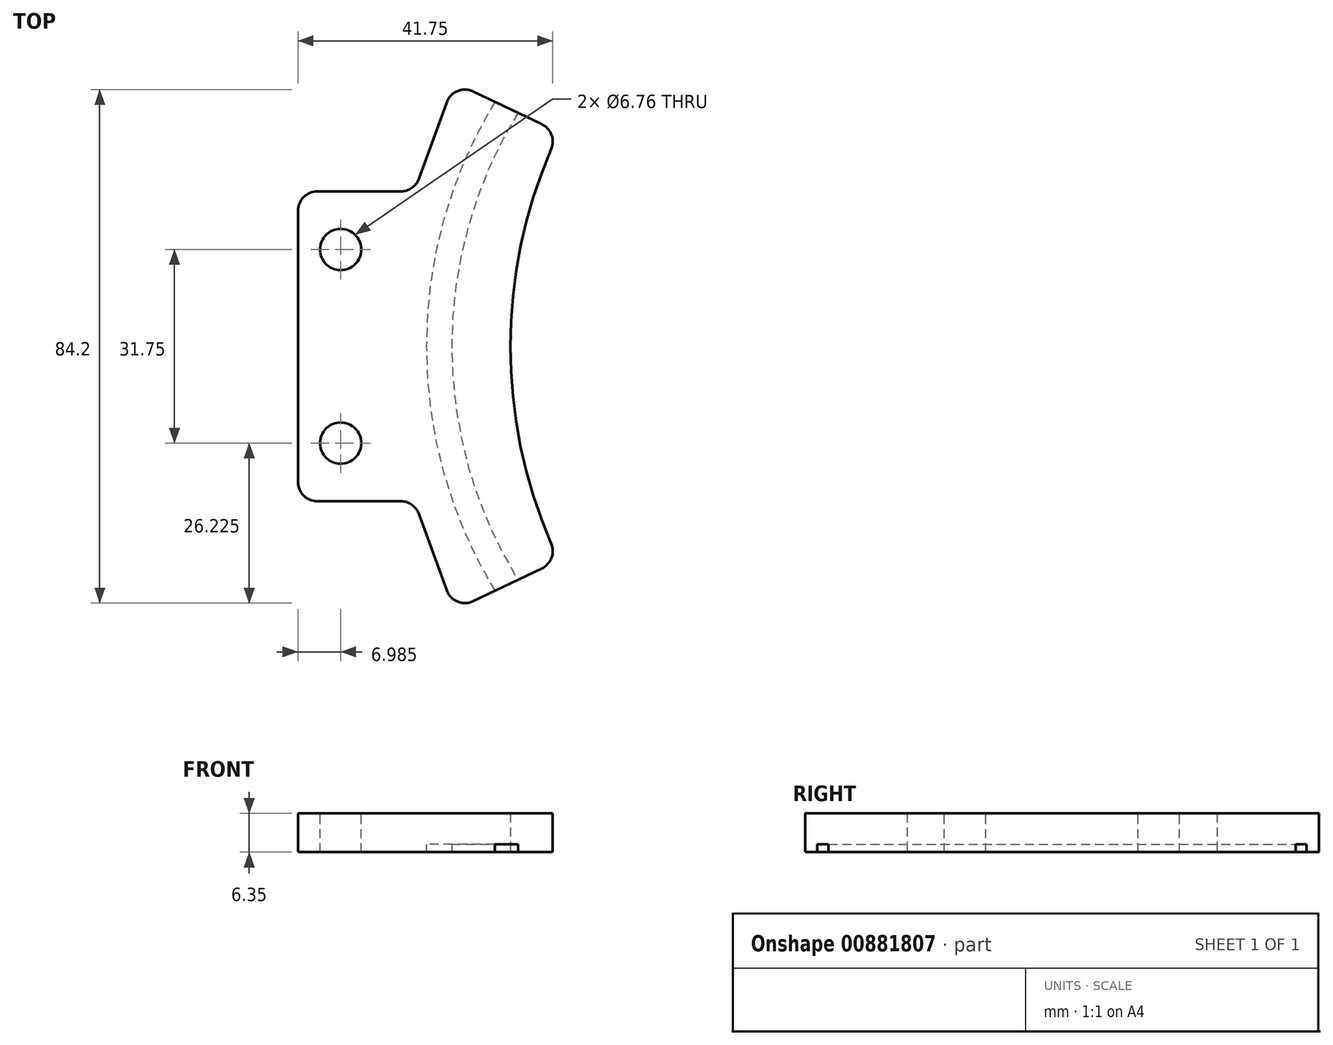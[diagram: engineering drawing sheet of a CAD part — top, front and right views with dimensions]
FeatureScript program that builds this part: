
annotation { "Feature Type Name" : "Feature", "Feature Type Description" : "" }
export const myFeature = defineFeature(function(context is Context, id is Id, definition is map)
    precondition{}
    {
        {
            var Q0;
            Q0=qCreatedBy(makeId("Top.planeOp"),FACE);
            var sketch = newSketch(context, id + "F0", { "sketchPlane" : qUnion([Q0])});
            skLineSegment(sketch, "E0", {"start": v(0, 25.4) * mm, "end": v(19.05, 25.4) * mm});
            skLineSegment(sketch, "E1", {"start": v(0, 25.4) * mm, "end": v(0, -25.4) * mm});
            skLineSegment(sketch, "E2", {"start": v(0, -25.4) * mm, "end": v(19.05, -25.4) * mm});
            skPoint(sketch, "E3", {"position": v(0, 0) * mm});
            skArc(sketch, "E4", {"start": v(42.76, 35.1) * mm, "mid": v(34.81, 0) * mm, "end": v(42.76, -35.1) * mm});
            skLineSegment(sketch, "E5", {"start": v(42.76, -35.1) * mm, "end": v(25.57, -43.3) * mm});
            skLineSegment(sketch, "E6", {"start": v(25.57, -43.3) * mm, "end": v(19.05, -25.4) * mm});
            skLineSegment(sketch, "E7", {"start": v(42.76, 35.1) * mm, "end": v(25.57, 43.3) * mm});
            skLineSegment(sketch, "E8", {"start": v(25.57, 43.3) * mm, "end": v(19.05, 25.4) * mm});
            skLineSegment(sketch, "E9", {"start": v(0, 0) * mm, "end": v(116.3, 0) * mm, "construction": true});
            skLineSegment(sketch, "E10", {"start": v(42.76, 35.1) * mm, "end": v(45.5, 40.83) * mm, "construction": true});
            skSolve(sketch);
        }
        {
            var Q0;
            Q0=makeQuery(id+"F0.imprint","IMPRINT",FACE,{"disambiguationData":[TD([[makeQuery(id+"F0.imprint","IMPRINT",EDGE,{"derivedFrom":sQuery(id+"F0.wireOp",EDGE,"E0")}),-1.0]])]});
            extrude(context, id + "F1", {"entities" : qUnion([Q0]), "depth" : 6.35 * mm, "offsetDistance" : 25.4 * mm});
        }
        {
            var Q0;
            Q0=makeQuery(id+"F1.opExtrude","CAP_FACE",FACE,{"disambiguationData":[OSD([sQuery(id+"F0.wireOp",EDGE,"E0"),sQuery(id+"F0.wireOp",EDGE,"E1"),sQuery(id+"F0.wireOp",EDGE,"E2"),sQuery(id+"F0.wireOp",EDGE,"E4"),sQuery(id+"F0.wireOp",EDGE,"E5"),sQuery(id+"F0.wireOp",EDGE,"E6"),sQuery(id+"F0.wireOp",EDGE,"E7"),sQuery(id+"F0.wireOp",EDGE,"E8")])],"isStart":true});
            var sketch = newSketch(context, id + "F2", { "sketchPlane" : qUnion([Q0])});
            skArc(sketch, "E11", {"start": v(34.16, 39.2) * mm, "mid": v(23.13, 0) * mm, "end": v(34.16, -39.2) * mm, "construction": true});
            skArc(sketch, "E12.0", {"start": v(32.27, 40.1) * mm, "mid": v(21.04, 0) * mm, "end": v(32.27, -40.1) * mm});
            skArc(sketch, "E13.0", {"start": v(36.05, 38.3) * mm, "mid": v(25.2, 0) * mm, "end": v(36.05, -38.3) * mm});
            skLineSegment(sketch, "E14", {"start": v(32.27, 40.1) * mm, "end": v(36.05, 38.3) * mm});
            skLineSegment(sketch, "E15", {"start": v(32.27, -40.1) * mm, "end": v(36.05, -38.3) * mm});
            skSolve(sketch);
        }
        {
            var Q0;
            Q0=makeQuery(id+"F2.imprint","IMPRINT",FACE,{"disambiguationData":[TD([[makeQuery(id+"F2.imprint","IMPRINT",EDGE,{"derivedFrom":sQuery(id+"F2.wireOp",EDGE,"E12.0")}),1.0]])]});
            extrude(context, id + "F3", {"entities" : qUnion([Q0]), "operationType" : NewBodyOperationType.REMOVE, "oppositeDirection" : true, "depth" : 1.27 * mm, "offsetDistance" : 25.4 * mm});
        }
        {
            var Q0;
            Q0=makeQuery(id+"F1.opExtrude","CAP_FACE",FACE,{"disambiguationData":[OSD([sQuery(id+"F0.wireOp",EDGE,"E0"),sQuery(id+"F0.wireOp",EDGE,"E1"),sQuery(id+"F0.wireOp",EDGE,"E2"),sQuery(id+"F0.wireOp",EDGE,"E4"),sQuery(id+"F0.wireOp",EDGE,"E5"),sQuery(id+"F0.wireOp",EDGE,"E6"),sQuery(id+"F0.wireOp",EDGE,"E7"),sQuery(id+"F0.wireOp",EDGE,"E8")])],"isStart":false});
            var sketch = newSketch(context, id + "F4", { "sketchPlane" : qUnion([Q0])});
            skCircle(sketch, "E16", {"center": v(6.99, 15.88) * mm, "radius": 3.38 * mm});
            skCircle(sketch, "E17", {"center": v(6.99, -15.87) * mm, "radius": 3.38 * mm});
            skLineSegment(sketch, "E18", {"start": v(0, 0) * mm, "end": v(34.81, 0) * mm, "construction": true});
            skSolve(sketch);
        }
        {
            var Q0;
            Q0=makeQuery(id+"F4.imprint","IMPRINT",FACE,{"disambiguationData":[TD([[makeQuery(id+"F4.imprint","IMPRINT",EDGE,{"derivedFrom":sQuery(id+"F4.wireOp",EDGE,"E16")}),1.0]])]});
            var Q1;
            Q1=makeQuery(id+"F4.imprint","IMPRINT",FACE,{"disambiguationData":[TD([[makeQuery(id+"F4.imprint","IMPRINT",EDGE,{"derivedFrom":sQuery(id+"F4.wireOp",EDGE,"E17")}),1.0]])]});
            extrude(context, id + "F5", {"entities" : qUnion([Q0, Q1]), "operationType" : NewBodyOperationType.REMOVE, "endBound" : BoundingType.THROUGH_ALL, "oppositeDirection" : true, "depth" : 25.4 * mm, "offsetDistance" : 25.4 * mm});
        }
        {
            var Q0;
            Q0=makeQuery(id+"F1.opExtrude","SWEPT_EDGE",EDGE,{"disambiguationData":[OSD([sQuery(id+"F0.wireOp",EDGE,"E1"),sQuery(id+"F0.wireOp",EDGE,"E2")])]});
            var Q1;
            Q1=makeQuery(id+"F1.opExtrude","SWEPT_EDGE",EDGE,{"disambiguationData":[OSD([sQuery(id+"F0.wireOp",EDGE,"E2"),sQuery(id+"F0.wireOp",EDGE,"E6")])]});
            var Q2;
            Q2=makeQuery(id+"F1.opExtrude","SWEPT_EDGE",EDGE,{"disambiguationData":[OSD([sQuery(id+"F0.wireOp",EDGE,"E5"),sQuery(id+"F0.wireOp",EDGE,"E6")])]});
            var Q3;
            Q3=makeQuery(id+"F1.opExtrude","SWEPT_EDGE",EDGE,{"disambiguationData":[OSD([sQuery(id+"F0.wireOp",EDGE,"E4"),sQuery(id+"F0.wireOp",EDGE,"E5")])]});
            var Q4;
            Q4=makeQuery(id+"F1.opExtrude","SWEPT_EDGE",EDGE,{"disambiguationData":[OSD([sQuery(id+"F0.wireOp",EDGE,"E0"),sQuery(id+"F0.wireOp",EDGE,"E1")])]});
            var Q5;
            Q5=makeQuery(id+"F1.opExtrude","SWEPT_EDGE",EDGE,{"disambiguationData":[OSD([sQuery(id+"F0.wireOp",EDGE,"E4"),sQuery(id+"F0.wireOp",EDGE,"E7")])]});
            var Q6;
            Q6=makeQuery(id+"F1.opExtrude","SWEPT_EDGE",EDGE,{"disambiguationData":[OSD([sQuery(id+"F0.wireOp",EDGE,"E7"),sQuery(id+"F0.wireOp",EDGE,"E8")])]});
            var Q7;
            Q7=makeQuery(id+"F1.opExtrude","SWEPT_EDGE",EDGE,{"disambiguationData":[OSD([sQuery(id+"F0.wireOp",EDGE,"E0"),sQuery(id+"F0.wireOp",EDGE,"E8")])]});
            fillet(context, id + "F6", {"entities" : qUnion([Q0, Q1, Q2, Q3, Q4, Q5, Q6, Q7]), "radius" : 3.17 * mm, "tangentPropagation" : true, "allowEdgeOverflow" : false});
        }
    });
